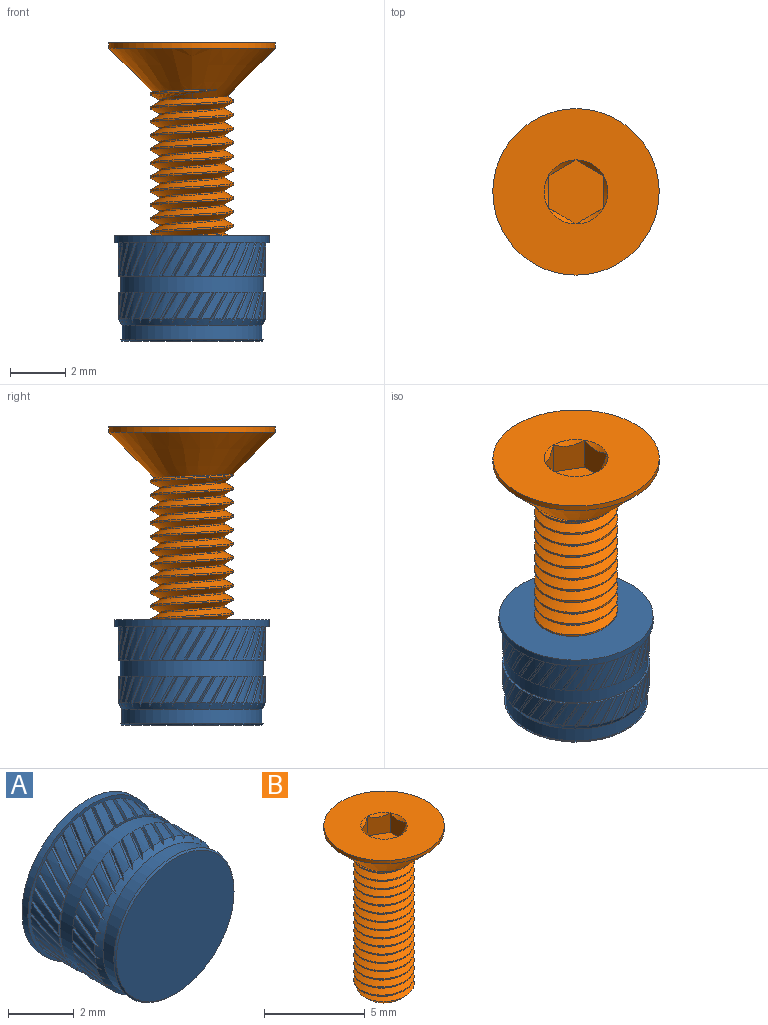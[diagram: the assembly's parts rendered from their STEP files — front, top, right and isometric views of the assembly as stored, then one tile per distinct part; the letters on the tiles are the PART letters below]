
ASSEMBLY  parts=2 mates=1
PART A: 227 faces, bbox 5.6x3.8x5.6 mm
  f0: cylinder r=2.58mm len=5.16mm, axis (0,1,0), area 9.3mm2, adj f225,f226
  f1: cone r=2.58mm half-angle=45deg, axis (0,1,0), area 1.2mm2, adj f151,f152
  f2: cone r=2.65mm half-angle=30deg, axis (0,1,0), area 3.9mm2, adj f5,f7,f8,f9,f10,f11,f12,f13
  f3: cylinder r=2.78mm len=5.56mm, axis (0,1,0), area 4.4mm2, adj f149,f150
  f4: cylinder r=2.65mm len=1.2mm, axis (0,1,0), area 0.4mm2, adj f149,f153,f156,f226
  f5: cylinder r=2.52mm len=5.05mm, axis (0,1,0), area 8.3mm2, adj f2,f151
  f6: cylinder r=2.65mm len=1.2mm, axis (0,1,0), area 0.4mm2, adj f149,f155,f158,f226
  f7: cylinder r=2.65mm len=0.97mm, axis (0,1,0), area 0.3mm2, adj f2,f47,f50,f225
  f8: cylinder r=2.65mm len=0.97mm, axis (0,1,0), area 0.3mm2, adj f2,f49,f51,f225
  f9: cylinder r=2.65mm len=0.97mm, axis (0,1,0), area 0.3mm2, adj f2,f111,f113,f225
  f10: cylinder r=2.65mm len=0.97mm, axis (0,1,0), area 0.3mm2, adj f2,f44,f114,f225
  f11: cylinder r=2.65mm len=0.97mm, axis (0,1,0), area 0.3mm2, adj f2,f109,f112,f225
  f12: cylinder r=2.65mm len=0.97mm, axis (0,1,0), area 0.3mm2, adj f2,f108,f110,f225
  f13: cylinder r=2.65mm len=0.97mm, axis (0,1,0), area 0.3mm2, adj f2,f103,f105,f225
  f14: cylinder r=2.65mm len=0.97mm, axis (0,1,0), area 0.3mm2, adj f2,f106,f107,f225
  f15: cylinder r=2.65mm len=0.97mm, axis (0,1,0), area 0.3mm2, adj f2,f101,f104,f225
  f16: cylinder r=2.65mm len=0.97mm, axis (0,1,0), area 0.3mm2, adj f2,f99,f102,f225
  f17: cylinder r=2.65mm len=0.97mm, axis (0,1,0), area 0.3mm2, adj f2,f97,f100,f225
  f18: cylinder r=2.65mm len=0.97mm, axis (0,1,0), area 0.3mm2, adj f2,f93,f95,f225
  f19: cylinder r=2.65mm len=0.97mm, axis (0,1,0), area 0.3mm2, adj f2,f96,f98,f225
  f20: cylinder r=2.65mm len=0.97mm, axis (0,1,0), area 0.3mm2, adj f2,f91,f94,f225
  f21: cylinder r=2.65mm len=0.97mm, axis (0,1,0), area 0.3mm2, adj f2,f90,f92,f225
  f22: cylinder r=2.65mm len=0.97mm, axis (0,1,0), area 0.3mm2, adj f2,f88,f89,f225
  f23: cylinder r=2.65mm len=0.97mm, axis (0,1,0), area 0.3mm2, adj f2,f85,f87,f225
  f24: cylinder r=2.65mm len=0.97mm, axis (0,1,0), area 0.3mm2, adj f2,f83,f86,f225
  f25: cylinder r=2.65mm len=0.97mm, axis (0,1,0), area 0.3mm2, adj f2,f81,f84,f225
  f26: cylinder r=2.65mm len=0.97mm, axis (0,1,0), area 0.3mm2, adj f2,f79,f82,f225
  f27: cylinder r=2.65mm len=0.97mm, axis (0,1,0), area 0.3mm2, adj f2,f78,f80,f225
  f28: cylinder r=2.65mm len=0.97mm, axis (0,1,0), area 0.3mm2, adj f2,f75,f77,f225
  f29: cylinder r=2.65mm len=0.97mm, axis (0,1,0), area 0.3mm2, adj f2,f73,f76,f225
  f30: cylinder r=2.65mm len=0.97mm, axis (0,1,0), area 0.3mm2, adj f2,f72,f74,f225
  f31: cylinder r=2.65mm len=0.97mm, axis (0,1,0), area 0.3mm2, adj f2,f67,f69,f225
  f32: cylinder r=2.65mm len=0.97mm, axis (0,1,0), area 0.3mm2, adj f2,f70,f71,f225
  f33: cylinder r=2.65mm len=0.97mm, axis (0,1,0), area 0.3mm2, adj f2,f65,f68,f225
  f34: cylinder r=2.65mm len=0.97mm, axis (0,1,0), area 0.3mm2, adj f2,f63,f66,f225
  f35: cylinder r=2.65mm len=0.97mm, axis (0,1,0), area 0.3mm2, adj f2,f61,f64,f225
  f36: cylinder r=2.65mm len=0.97mm, axis (0,1,0), area 0.3mm2, adj f2,f57,f59,f225
  f37: cylinder r=2.65mm len=0.97mm, axis (0,1,0), area 0.3mm2, adj f2,f60,f62,f225
  f38: cylinder r=2.65mm len=0.97mm, axis (0,1,0), area 0.3mm2, adj f2,f55,f58,f225
  f39: cylinder r=2.65mm len=0.97mm, axis (0,1,0), area 0.3mm2, adj f2,f52,f53,f225
  f40: cylinder r=2.65mm len=0.97mm, axis (0,1,0), area 0.3mm2, adj f2,f54,f56,f225
  f41: cylinder r=2.65mm len=0.97mm, axis (0,1,0), area 0.3mm2, adj f2,f45,f48,f225
  f42: cylinder r=2.65mm len=0.97mm, axis (0,1,0), area 0.3mm2, adj f2,f43,f46,f225
  f43: bspline ~1.08x0.57mm, area 0.1mm2, adj f2,f42,f44,f225
  f44: bspline ~1.21x0.69mm, area 0.1mm2, adj f2,f10,f43,f225
  f45: bspline ~1.08x0.63mm, area 0.1mm2, adj f2,f41,f46,f225
  f46: bspline ~1.21x0.74mm, area 0.1mm2, adj f2,f42,f45,f225
  f47: bspline ~1.08x0.67mm, area 0.1mm2, adj f2,f7,f48,f225
  f48: bspline ~1.21x0.76mm, area 0.1mm2, adj f2,f41,f47,f225
  f49: bspline ~1.08x0.69mm, area 0.1mm2, adj f2,f8,f50,f225
  f50: bspline ~1.21x0.76mm, area 0.1mm2, adj f2,f7,f49,f225
  f51: bspline ~1.31x0.79mm, area 0.1mm2, adj f2,f8,f52,f225
  f52: bspline ~1.31x0.81mm, area 0.1mm2, adj f2,f39,f51,f225
  f53: bspline ~1.31x0.74mm, area 0.1mm2, adj f2,f39,f54,f225
  f54: bspline ~1.31x0.78mm, area 0.1mm2, adj f2,f40,f53,f225
  f55: bspline ~1.21x0.67mm, area 0.1mm2, adj f2,f38,f56,f225
  f56: bspline ~1.21x0.62mm, area 0.1mm2, adj f2,f40,f55,f225
  f57: bspline ~1.21x0.6mm, area 0.1mm2, adj f2,f36,f58,f225
  f58: bspline ~1.21x0.54mm, area 0.1mm2, adj f2,f38,f57,f225
  f59: bspline ~1.31x0.67mm, area 0.1mm2, adj f2,f36,f60,f225
  f60: bspline ~1.31x0.6mm, area 0.1mm2, adj f2,f37,f59,f225
  f61: bspline ~1.08x0.57mm, area 0.1mm2, adj f2,f35,f62,f225
  f62: bspline ~1.21x0.69mm, area 0.1mm2, adj f2,f37,f61,f225
  f63: bspline ~1.08x0.63mm, area 0.1mm2, adj f2,f34,f64,f225
  f64: bspline ~1.21x0.74mm, area 0.1mm2, adj f2,f35,f63,f225
  f65: bspline ~1.08x0.67mm, area 0.1mm2, adj f2,f33,f66,f225
  f66: bspline ~1.21x0.76mm, area 0.1mm2, adj f2,f34,f65,f225
  f67: bspline ~1.08x0.69mm, area 0.1mm2, adj f2,f31,f68,f225
  f68: bspline ~1.21x0.76mm, area 0.1mm2, adj f2,f33,f67,f225
  f69: bspline ~1.31x0.79mm, area 0.1mm2, adj f2,f31,f70,f225
  f70: bspline ~1.31x0.81mm, area 0.1mm2, adj f2,f32,f69,f225
  f71: bspline ~1.31x0.74mm, area 0.1mm2, adj f2,f32,f72,f225
  f72: bspline ~1.31x0.78mm, area 0.1mm2, adj f2,f30,f71,f225
  f73: bspline ~1.21x0.67mm, area 0.1mm2, adj f2,f29,f74,f225
  f74: bspline ~1.21x0.62mm, area 0.1mm2, adj f2,f30,f73,f225
  f75: bspline ~1.21x0.6mm, area 0.1mm2, adj f2,f28,f76,f225
  f76: bspline ~1.21x0.54mm, area 0.1mm2, adj f2,f29,f75,f225
  f77: bspline ~1.31x0.67mm, area 0.1mm2, adj f2,f28,f78,f225
  f78: bspline ~1.31x0.6mm, area 0.1mm2, adj f2,f27,f77,f225
  f79: bspline ~1.08x0.57mm, area 0.1mm2, adj f2,f26,f80,f225
  f80: bspline ~1.21x0.69mm, area 0.1mm2, adj f2,f27,f79,f225
  f81: bspline ~1.08x0.63mm, area 0.1mm2, adj f2,f25,f82,f225
  f82: bspline ~1.21x0.74mm, area 0.1mm2, adj f2,f26,f81,f225
  f83: bspline ~1.08x0.67mm, area 0.1mm2, adj f2,f24,f84,f225
  f84: bspline ~1.21x0.76mm, area 0.1mm2, adj f2,f25,f83,f225
  f85: bspline ~1.08x0.69mm, area 0.1mm2, adj f2,f23,f86,f225
  f86: bspline ~1.21x0.76mm, area 0.1mm2, adj f2,f24,f85,f225
  f87: bspline ~1.31x0.79mm, area 0.1mm2, adj f2,f23,f88,f225
  f88: bspline ~1.31x0.81mm, area 0.1mm2, adj f2,f22,f87,f225
  f89: bspline ~1.31x0.74mm, area 0.1mm2, adj f2,f22,f90,f225
  f90: bspline ~1.31x0.78mm, area 0.1mm2, adj f2,f21,f89,f225
  f91: bspline ~1.21x0.67mm, area 0.1mm2, adj f2,f20,f92,f225
  f92: bspline ~1.21x0.62mm, area 0.1mm2, adj f2,f21,f91,f225
  f93: bspline ~1.21x0.6mm, area 0.1mm2, adj f2,f18,f94,f225
  f94: bspline ~1.21x0.54mm, area 0.1mm2, adj f2,f20,f93,f225
  f95: bspline ~1.31x0.67mm, area 0.1mm2, adj f2,f18,f96,f225
  f96: bspline ~1.31x0.6mm, area 0.1mm2, adj f2,f19,f95,f225
  f97: bspline ~1.08x0.57mm, area 0.1mm2, adj f2,f17,f98,f225
  f98: bspline ~1.21x0.69mm, area 0.1mm2, adj f2,f19,f97,f225
  f99: bspline ~1.08x0.63mm, area 0.1mm2, adj f2,f16,f100,f225
  f100: bspline ~1.21x0.74mm, area 0.1mm2, adj f2,f17,f99,f225
  f101: bspline ~1.08x0.67mm, area 0.1mm2, adj f2,f15,f102,f225
  f102: bspline ~1.21x0.76mm, area 0.1mm2, adj f2,f16,f101,f225
  f103: bspline ~1.08x0.69mm, area 0.1mm2, adj f2,f13,f104,f225
  f104: bspline ~1.21x0.76mm, area 0.1mm2, adj f2,f15,f103,f225
  f105: bspline ~1.31x0.79mm, area 0.1mm2, adj f2,f13,f106,f225
  f106: bspline ~1.31x0.81mm, area 0.1mm2, adj f2,f14,f105,f225
  f107: bspline ~1.31x0.74mm, area 0.1mm2, adj f2,f14,f108,f225
  f108: bspline ~1.31x0.78mm, area 0.1mm2, adj f2,f12,f107,f225
  f109: bspline ~1.21x0.67mm, area 0.1mm2, adj f2,f11,f110,f225
  f110: bspline ~1.21x0.62mm, area 0.1mm2, adj f2,f12,f109,f225
  f111: bspline ~1.21x0.6mm, area 0.1mm2, adj f2,f9,f112,f225
  f112: bspline ~1.21x0.54mm, area 0.1mm2, adj f2,f11,f111,f225
  f113: bspline ~1.31x0.67mm, area 0.1mm2, adj f2,f9,f114,f225
  f114: bspline ~1.31x0.6mm, area 0.1mm2, adj f2,f10,f113,f225
  f115: cylinder r=2.65mm len=1.2mm, axis (0,1,0), area 0.4mm2, adj f149,f221,f224,f226
  f116: cylinder r=2.65mm len=1.2mm, axis (0,1,0), area 0.4mm2, adj f149,f154,f223,f226
  f117: cylinder r=2.65mm len=1.2mm, axis (0,1,0), area 0.4mm2, adj f149,f219,f222,f226
  f118: cylinder r=2.65mm len=1.2mm, axis (0,1,0), area 0.4mm2, adj f149,f217,f220,f226
  f119: cylinder r=2.65mm len=1.2mm, axis (0,1,0), area 0.4mm2, adj f149,f213,f216,f226
  f120: cylinder r=2.65mm len=1.2mm, axis (0,1,0), area 0.4mm2, adj f149,f215,f218,f226
  f121: cylinder r=2.65mm len=1.2mm, axis (0,1,0), area 0.4mm2, adj f149,f211,f214,f226
  f122: cylinder r=2.65mm len=1.2mm, axis (0,1,0), area 0.4mm2, adj f149,f209,f212,f226
  f123: cylinder r=2.65mm len=1.2mm, axis (0,1,0), area 0.4mm2, adj f149,f207,f210,f226
  f124: cylinder r=2.65mm len=1.2mm, axis (0,1,0), area 0.4mm2, adj f149,f203,f206,f226
  f125: cylinder r=2.65mm len=1.2mm, axis (0,1,0), area 0.4mm2, adj f149,f205,f208,f226
  f126: cylinder r=2.65mm len=1.2mm, axis (0,1,0), area 0.4mm2, adj f149,f201,f204,f226
  f127: cylinder r=2.65mm len=1.2mm, axis (0,1,0), area 0.4mm2, adj f149,f199,f202,f226
  f128: cylinder r=2.65mm len=1.2mm, axis (0,1,0), area 0.4mm2, adj f149,f197,f200,f226
  f129: cylinder r=2.65mm len=1.2mm, axis (0,1,0), area 0.4mm2, adj f149,f195,f198,f226
  f130: cylinder r=2.65mm len=1.2mm, axis (0,1,0), area 0.4mm2, adj f149,f193,f196,f226
  f131: cylinder r=2.65mm len=1.2mm, axis (0,1,0), area 0.4mm2, adj f149,f191,f194,f226
  f132: cylinder r=2.65mm len=1.2mm, axis (0,1,0), area 0.4mm2, adj f149,f189,f192,f226
  f133: cylinder r=2.65mm len=1.2mm, axis (0,1,0), area 0.4mm2, adj f149,f187,f190,f226
  f134: cylinder r=2.65mm len=1.2mm, axis (0,1,0), area 0.4mm2, adj f149,f185,f188,f226
  f135: cylinder r=2.65mm len=1.2mm, axis (0,1,0), area 0.4mm2, adj f149,f183,f186,f226
  f136: cylinder r=2.65mm len=1.2mm, axis (0,1,0), area 0.4mm2, adj f149,f181,f184,f226
  f137: cylinder r=2.65mm len=1.2mm, axis (0,1,0), area 0.4mm2, adj f149,f177,f180,f226
  f138: cylinder r=2.65mm len=1.2mm, axis (0,1,0), area 0.4mm2, adj f149,f179,f182,f226
  f139: cylinder r=2.65mm len=1.2mm, axis (0,1,0), area 0.4mm2, adj f149,f175,f178,f226
  f140: cylinder r=2.65mm len=1.2mm, axis (0,1,0), area 0.4mm2, adj f149,f173,f176,f226
  f141: cylinder r=2.65mm len=1.2mm, axis (0,1,0), area 0.4mm2, adj f149,f171,f174,f226
  f142: cylinder r=2.65mm len=1.2mm, axis (0,1,0), area 0.4mm2, adj f149,f167,f170,f226
  f143: cylinder r=2.65mm len=1.2mm, axis (0,1,0), area 0.4mm2, adj f149,f169,f172,f226
  f144: cylinder r=2.65mm len=1.2mm, axis (0,1,0), area 0.4mm2, adj f149,f165,f168,f226
  f145: cylinder r=2.65mm len=1.2mm, axis (0,1,0), area 0.4mm2, adj f149,f161,f164,f226
  f146: cylinder r=2.65mm len=1.2mm, axis (0,1,0), area 0.4mm2, adj f149,f163,f166,f226
  f147: cylinder r=2.65mm len=1.2mm, axis (0,1,0), area 0.4mm2, adj f149,f159,f162,f226
  f148: cylinder r=2.65mm len=1.2mm, axis (0,1,0), area 0.4mm2, adj f149,f157,f160,f226
  f149: plane 5.56x5.56mm, normal (0,-1,0), area 2.3mm2, adj f3,f4,f6,f115,f116,f117,f118,f119
  f150: plane 5.56x5.56mm, normal (0,1,0), area 24.3mm2, adj f3
  f151: plane 5.16x5.16mm, normal (0,1,0), area 0.9mm2, adj f1,f5
  f152: plane 5.05x5.05mm, normal (0,-1,0), area 20mm2, adj f1
  f153: bspline ~1.31x0.79mm, area 0.1mm2, adj f4,f149,f154,f226
  f154: bspline ~1.31x0.81mm, area 0.1mm2, adj f116,f149,f153,f226
  f155: bspline ~1.31x0.81mm, area 0.1mm2, adj f6,f149,f156,f226
  f156: bspline ~1.31x0.81mm, area 0.1mm2, adj f4,f149,f155,f226
  f157: bspline ~1.31x0.81mm, area 0.1mm2, adj f148,f149,f158,f226
  f158: bspline ~1.31x0.78mm, area 0.1mm2, adj f6,f149,f157,f226
  f159: bspline ~1.2x0.71mm, area 0.1mm2, adj f147,f149,f160,f226
  f160: bspline ~1.31x0.73mm, area 0.1mm2, adj f148,f149,f159,f226
  f161: bspline ~1.31x0.72mm, area 0.1mm2, adj f145,f149,f162,f226
  f162: bspline ~1.31x0.66mm, area 0.1mm2, adj f147,f149,f161,f226
  f163: bspline ~1.31x0.64mm, area 0.1mm2, adj f146,f149,f164,f226
  f164: bspline ~1.31x0.58mm, area 0.1mm2, adj f145,f149,f163,f226
  f165: bspline ~1.2x0.56mm, area 0.1mm2, adj f144,f149,f166,f226
  f166: bspline ~1.31x0.67mm, area 0.1mm2, adj f146,f149,f165,f226
  f167: bspline ~1.2x0.64mm, area 0.1mm2, adj f142,f149,f168,f226
  f168: bspline ~1.31x0.74mm, area 0.1mm2, adj f144,f149,f167,f226
  f169: bspline ~1.31x0.75mm, area 0.1mm2, adj f143,f149,f170,f226
  f170: bspline ~1.31x0.79mm, area 0.1mm2, adj f142,f149,f169,f226
  f171: bspline ~1.31x0.79mm, area 0.1mm2, adj f141,f149,f172,f226
  f172: bspline ~1.31x0.81mm, area 0.1mm2, adj f143,f149,f171,f226
  f173: bspline ~1.31x0.81mm, area 0.1mm2, adj f140,f149,f174,f226
  f174: bspline ~1.31x0.81mm, area 0.1mm2, adj f141,f149,f173,f226
  f175: bspline ~1.31x0.81mm, area 0.1mm2, adj f139,f149,f176,f226
  f176: bspline ~1.31x0.78mm, area 0.1mm2, adj f140,f149,f175,f226
  f177: bspline ~1.2x0.71mm, area 0.1mm2, adj f137,f149,f178,f226
  f178: bspline ~1.31x0.73mm, area 0.1mm2, adj f139,f149,f177,f226
  f179: bspline ~1.31x0.72mm, area 0.1mm2, adj f138,f149,f180,f226
  f180: bspline ~1.31x0.66mm, area 0.1mm2, adj f137,f149,f179,f226
  f181: bspline ~1.31x0.64mm, area 0.1mm2, adj f136,f149,f182,f226
  f182: bspline ~1.31x0.58mm, area 0.1mm2, adj f138,f149,f181,f226
  f183: bspline ~1.2x0.56mm, area 0.1mm2, adj f135,f149,f184,f226
  f184: bspline ~1.31x0.67mm, area 0.1mm2, adj f136,f149,f183,f226
  f185: bspline ~1.2x0.64mm, area 0.1mm2, adj f134,f149,f186,f226
  f186: bspline ~1.31x0.74mm, area 0.1mm2, adj f135,f149,f185,f226
  f187: bspline ~1.31x0.75mm, area 0.1mm2, adj f133,f149,f188,f226
  f188: bspline ~1.31x0.79mm, area 0.1mm2, adj f134,f149,f187,f226
  f189: bspline ~1.31x0.79mm, area 0.1mm2, adj f132,f149,f190,f226
  f190: bspline ~1.31x0.81mm, area 0.1mm2, adj f133,f149,f189,f226
  f191: bspline ~1.31x0.81mm, area 0.1mm2, adj f131,f149,f192,f226
  f192: bspline ~1.31x0.81mm, area 0.1mm2, adj f132,f149,f191,f226
  f193: bspline ~1.31x0.81mm, area 0.1mm2, adj f130,f149,f194,f226
  f194: bspline ~1.31x0.78mm, area 0.1mm2, adj f131,f149,f193,f226
  f195: bspline ~1.2x0.71mm, area 0.1mm2, adj f129,f149,f196,f226
  f196: bspline ~1.31x0.73mm, area 0.1mm2, adj f130,f149,f195,f226
  f197: bspline ~1.31x0.72mm, area 0.1mm2, adj f128,f149,f198,f226
  f198: bspline ~1.31x0.66mm, area 0.1mm2, adj f129,f149,f197,f226
  f199: bspline ~1.31x0.64mm, area 0.1mm2, adj f127,f149,f200,f226
  f200: bspline ~1.31x0.58mm, area 0.1mm2, adj f128,f149,f199,f226
  f201: bspline ~1.2x0.56mm, area 0.1mm2, adj f126,f149,f202,f226
  f202: bspline ~1.31x0.67mm, area 0.1mm2, adj f127,f149,f201,f226
  f203: bspline ~1.2x0.64mm, area 0.1mm2, adj f124,f149,f204,f226
  f204: bspline ~1.31x0.74mm, area 0.1mm2, adj f126,f149,f203,f226
  f205: bspline ~1.31x0.75mm, area 0.1mm2, adj f125,f149,f206,f226
  f206: bspline ~1.31x0.79mm, area 0.1mm2, adj f124,f149,f205,f226
  f207: bspline ~1.31x0.79mm, area 0.1mm2, adj f123,f149,f208,f226
  f208: bspline ~1.31x0.81mm, area 0.1mm2, adj f125,f149,f207,f226
  f209: bspline ~1.31x0.81mm, area 0.1mm2, adj f122,f149,f210,f226
  f210: bspline ~1.31x0.81mm, area 0.1mm2, adj f123,f149,f209,f226
  f211: bspline ~1.31x0.81mm, area 0.1mm2, adj f121,f149,f212,f226
  f212: bspline ~1.31x0.78mm, area 0.1mm2, adj f122,f149,f211,f226
  f213: bspline ~1.2x0.71mm, area 0.1mm2, adj f119,f149,f214,f226
  f214: bspline ~1.31x0.73mm, area 0.1mm2, adj f121,f149,f213,f226
  f215: bspline ~1.31x0.72mm, area 0.1mm2, adj f120,f149,f216,f226
  f216: bspline ~1.31x0.66mm, area 0.1mm2, adj f119,f149,f215,f226
  f217: bspline ~1.31x0.64mm, area 0.1mm2, adj f118,f149,f218,f226
  f218: bspline ~1.31x0.58mm, area 0.1mm2, adj f120,f149,f217,f226
  f219: bspline ~1.2x0.56mm, area 0.1mm2, adj f117,f149,f220,f226
  f220: bspline ~1.31x0.67mm, area 0.1mm2, adj f118,f149,f219,f226
  f221: bspline ~1.2x0.64mm, area 0.1mm2, adj f115,f149,f222,f226
  f222: bspline ~1.31x0.74mm, area 0.1mm2, adj f117,f149,f221,f226
  f223: bspline ~1.31x0.75mm, area 0.1mm2, adj f116,f149,f224,f226
  f224: bspline ~1.31x0.79mm, area 0.1mm2, adj f115,f149,f223,f226
  f225: plane 5.31x5.31mm, normal (0,1,0), area 1.1mm2, adj f0,f7,f8,f9,f10,f11,f12,f13
  f226: plane 5.31x5.31mm, normal (0,-1,0), area 1.1mm2, adj f0,f4,f6,f115,f116,f117,f118,f119
PART B: 23 faces, bbox 6.4x6.4x10.6 mm
  f0: cone r=1.15mm half-angle=45deg, axis (0,0,1), area 0.1mm2, adj f10,f17
  f1: cone r=1.5mm half-angle=45deg, axis (0,0,1), area 31.8mm2, adj f2,f3,f6,f7,f8
  f2: cone r=1.5mm half-angle=45deg, axis (0,0,1), area 0.2mm2, adj f1,f5,f7,f8
  f3: cylinder r=3mm len=6mm, axis (0,0,1), area 3.8mm2, adj f1,f10
  f4: cone r=1.12mm half-angle=45deg, axis (0,0,1), area 2.4mm2, adj f5,f6,f7,f8,f9
  f5: cylinder r=1.18mm len=7.93mm, axis (0,0,1), area 7.3mm2, adj f2,f4,f7,f8
  f6: cylinder r=1.5mm len=7.93mm, axis (0,0,-1), area 9.3mm2, adj f1,f4,f7,f8
  f7: bspline ~8.69x3.46mm, area 50mm2, adj f1,f2,f4,f5,f6
  f8: bspline ~8.35x3.46mm, area 50mm2, adj f1,f2,f4,f5,f6
  f9: plane 2.25x2.25mm, normal (0,0,-1), area 4mm2, adj f4
  f10: plane 6x6mm, normal (0,0,1), area 24.1mm2, adj f0,f3,f11,f12,f13,f14,f15
  f11: cone r=1.15mm half-angle=45deg, axis (0,0,1), area 0mm2, adj f10,f18
  f12: cone r=1.15mm half-angle=45deg, axis (0,0,1), area 0mm2, adj f10,f19
  f13: cone r=1.15mm half-angle=45deg, axis (0,0,1), area 0mm2, adj f10,f20
  f14: cone r=1.15mm half-angle=45deg, axis (0,0,1), area 0mm2, adj f10,f21
  f15: cone r=1.15mm half-angle=45deg, axis (0,0,1), area 0mm2, adj f10,f22
  f16: plane 2.31x2mm, normal (0,0,1), area 3.5mm2, adj f17,f18,f19,f20,f21,f22
  f17: plane 1.3x1.27mm, normal (-1,0,0), area 1.3mm2, adj f0,f16,f18,f22
  f18: plane 1.63x1.44mm, normal (-0.5,-0.87,0), area 1.3mm2, adj f11,f16,f17,f19
  f19: plane 1.63x1.44mm, normal (0.5,-0.87,0), area 1.3mm2, adj f12,f16,f18,f20
  f20: plane 1.63x1.59mm, normal (1,0,0), area 1.3mm2, adj f13,f16,f19,f21
  f21: plane 1.63x1.44mm, normal (0.5,0.87,0), area 1.3mm2, adj f14,f16,f20,f22
  f22: plane 1.63x1.44mm, normal (-0.5,0.87,0), area 1.3mm2, adj f15,f16,f17,f21
PLACE A rot(axis=(1,0,0),90deg) t=(0,0,-6.96)mm
PLACE B at identity fixed
MATE fastened A.f2 <-> B.f3  axis (0,0,-1) through (0,0,-10.76)mm
